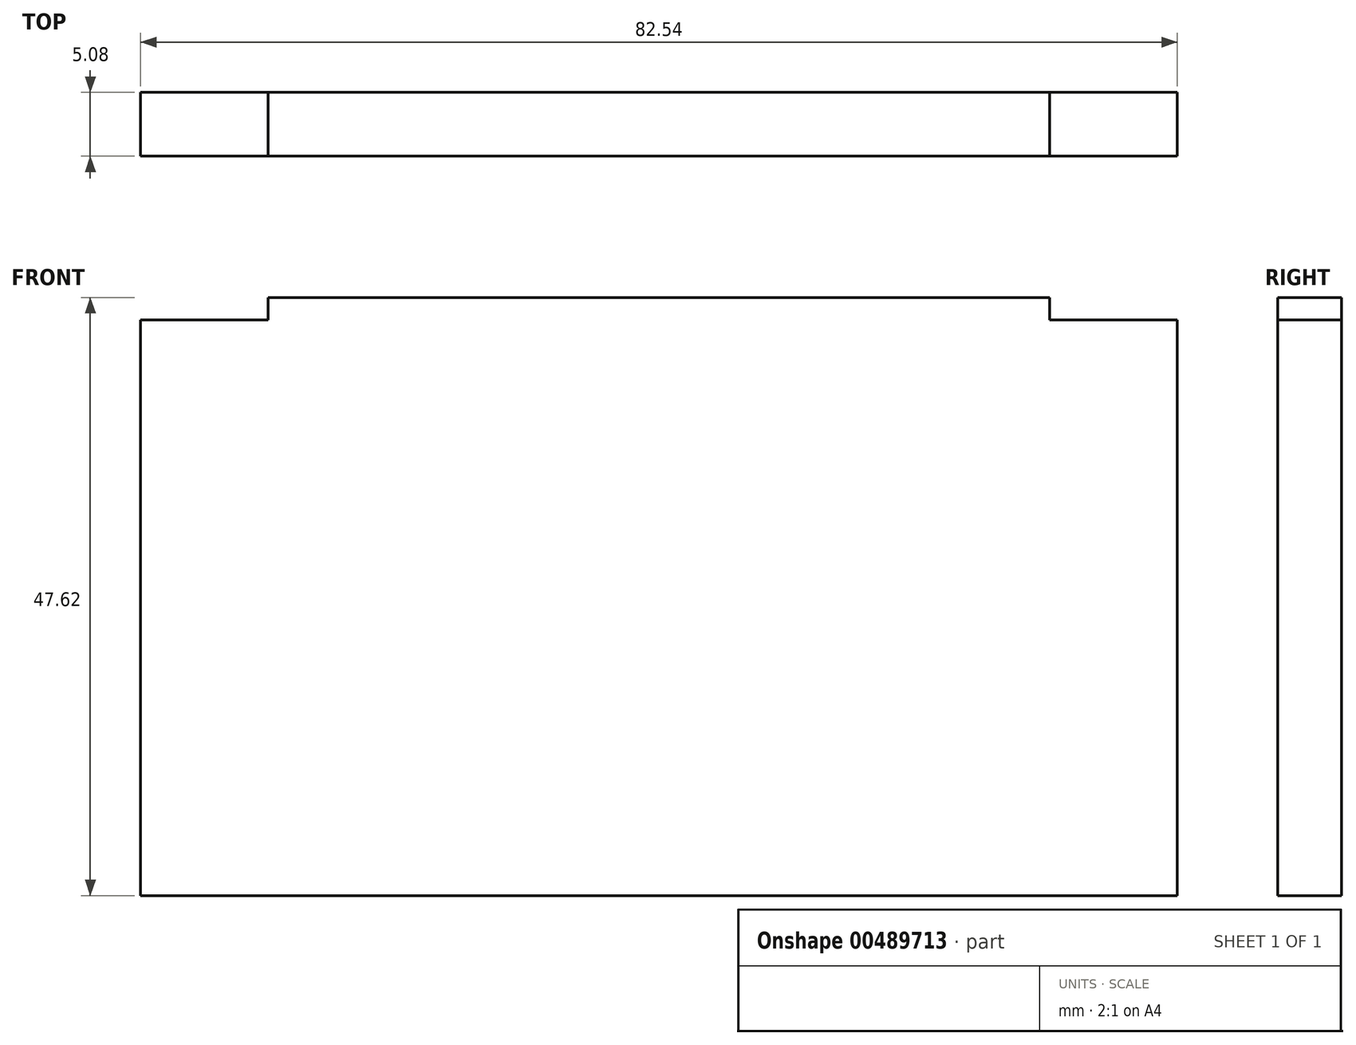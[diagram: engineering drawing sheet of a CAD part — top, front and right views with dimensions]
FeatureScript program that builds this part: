
annotation { "Feature Type Name" : "Feature", "Feature Type Description" : "" }
export const myFeature = defineFeature(function(context is Context, id is Id, definition is map)
    precondition{}
    {
        {
            var Q0;
            Q0=qCreatedBy(makeId("Front.planeOp"),FACE);
            var sketch = newSketch(context, id + "F0", { "sketchPlane" : qUnion([Q0])});
            skLineSegment(sketch, "E0.bottom", {"start": v(-31.12, 23.81) * mm, "end": v(31.12, 23.81) * mm});
            skLineSegment(sketch, "E0.top", {"start": v(-41.27, -23.81) * mm, "end": v(41.28, -23.81) * mm});
            skLineSegment(sketch, "E0.left", {"start": v(-41.28, 22.03) * mm, "end": v(-41.27, -23.81) * mm});
            skLineSegment(sketch, "E0.right", {"start": v(41.27, 22.03) * mm, "end": v(41.28, -23.81) * mm});
            skPoint(sketch, "E0.middle", {"position": v(0, 0) * mm});
            skLineSegment(sketch, "E1.bottom", {"start": v(0, 0) * mm, "end": v(0, 0) * mm});
            skLineSegment(sketch, "E1.top", {"start": v(0, -68.8) * mm, "end": v(0, -68.8) * mm});
            skLineSegment(sketch, "E1.left", {"start": v(0, 0) * mm, "end": v(0, -68.8) * mm});
            skLineSegment(sketch, "E1.right", {"start": v(0, 0) * mm, "end": v(0, -68.8) * mm});
            skPoint(sketch, "E1.middle", {"position": v(0, -34.4) * mm});
            skLineSegment(sketch, "E2.bottom", {"start": v(-41.28, 22.03) * mm, "end": v(-31.12, 22.03) * mm});
            skLineSegment(sketch, "E2.right", {"start": v(-31.12, 22.03) * mm, "end": v(-31.12, 23.81) * mm});
            skLineSegment(sketch, "E3.MirrorCS", {"start": v(41.28, 22.03) * mm, "end": v(31.12, 22.03) * mm});
            skLineSegment(sketch, "E4.MirrorCS", {"start": v(31.12, 22.03) * mm, "end": v(31.12, 23.81) * mm});
            skPoint(sketch, "E5.orphan", {"position": v(41.27, 23.81) * mm});
            skPoint(sketch, "E6.orphan", {"position": v(-41.28, 23.81) * mm});
            skSolve(sketch);
        }
        {
            var Q0;
            Q0=makeQuery(id+"F0.imprint","IMPRINT",FACE,{"disambiguationData":[TD([[makeQuery(id+"F0.imprint","IMPRINT",EDGE,{"derivedFrom":sQuery(id+"F0.wireOp",EDGE,"E0.bottom")}),-1.0]])]});
            extrude(context, id + "F1", {"entities" : qUnion([Q0]), "depth" : 5.08 * mm});
        }
    });
